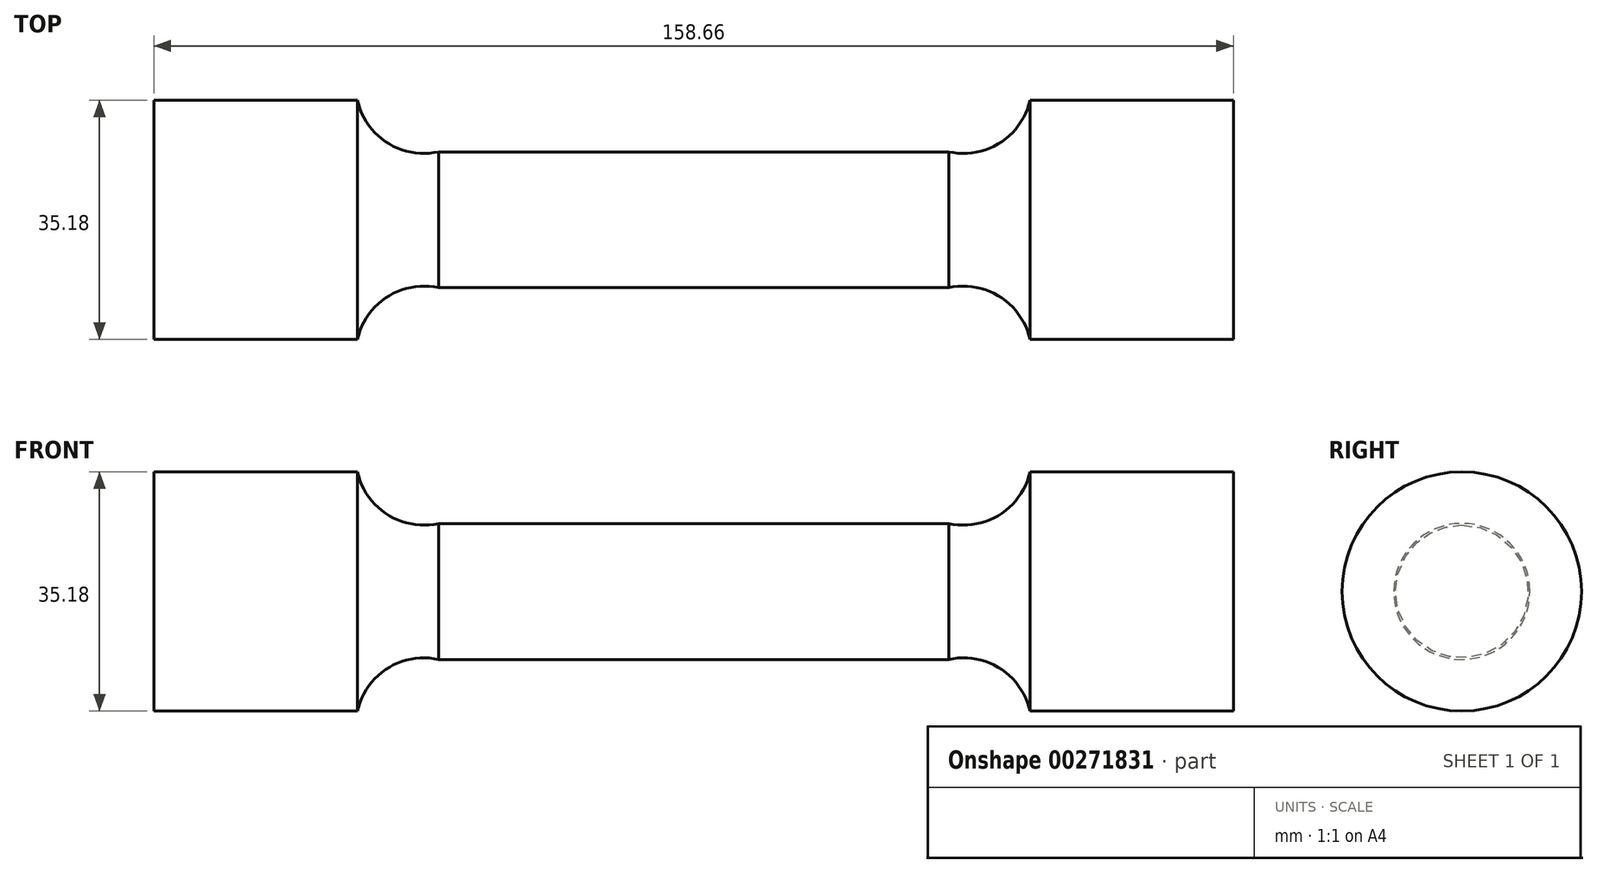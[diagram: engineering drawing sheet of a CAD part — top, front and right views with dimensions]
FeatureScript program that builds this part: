
annotation { "Feature Type Name" : "Feature", "Feature Type Description" : "" }
export const myFeature = defineFeature(function(context is Context, id is Id, definition is map)
    precondition{}
    {
        {
            var Q0;
            Q0=qCreatedBy(makeId("Front.planeOp"),FACE);
            var sketch = newSketch(context, id + "F0", { "sketchPlane" : qUnion([Q0])});
            skLineSegment(sketch, "E0", {"start": v(0, 10) * mm, "end": v(37.5, 10) * mm});
            skArc(sketch, "E1", {"start": v(37.5, 10) * mm, "mid": v(45.04, 11.33) * mm, "end": v(49.43, 17.6) * mm});
            skLineSegment(sketch, "E2", {"start": v(49.43, 17.6) * mm, "end": v(79.33, 17.6) * mm});
            skLineSegment(sketch, "E3", {"start": v(79.33, 17.6) * mm, "end": v(79.33, 0) * mm});
            skLineSegment(sketch, "E4.MirrorCS", {"start": v(0, 10) * mm, "end": v(-37.5, 10) * mm});
            skLineSegment(sketch, "E5.MirrorCS", {"start": v(-79.33, 17.6) * mm, "end": v(-79.33, 0) * mm});
            skLineSegment(sketch, "E6.MirrorCS", {"start": v(-49.43, 17.6) * mm, "end": v(-79.33, 17.6) * mm});
            skArc(sketch, "E7.MirrorCS", {"start": v(-37.5, 10) * mm, "mid": v(-45.04, 11.33) * mm, "end": v(-49.43, 17.6) * mm});
            skLineSegment(sketch, "E8", {"start": v(-79.33, 0) * mm, "end": v(79.33, 0) * mm});
            skSolve(sketch);
        }
        {
            var Q0;
            Q0 = qSketchRegion(id + "F0", true);
            var Q1;
            Q1=sQuery(id+"F0.wireOp",EDGE,"E8");
            revolve(context, id + "F1", {"entities" : qUnion([Q0]), "axis" : qUnion([Q1]), "revolveType" : RevolveType.FULL});
        }
    });
